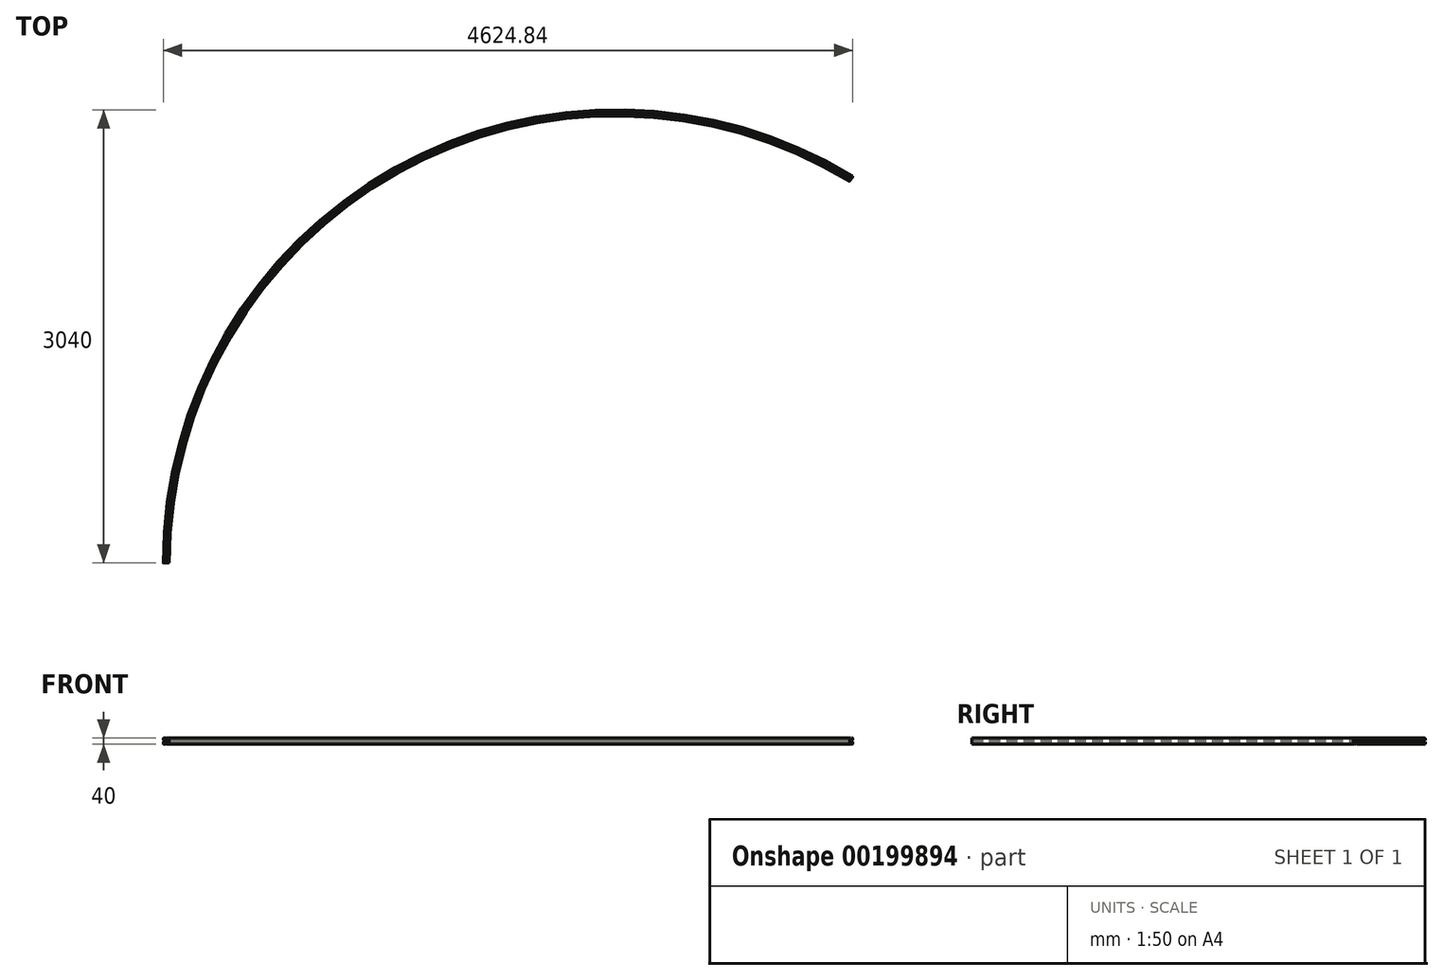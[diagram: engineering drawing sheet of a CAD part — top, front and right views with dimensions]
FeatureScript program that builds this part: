
annotation { "Feature Type Name" : "Feature", "Feature Type Description" : "" }
export const myFeature = defineFeature(function(context is Context, id is Id, definition is map)
    precondition{}
    {
        {
            var Q0;
            Q0=qCreatedBy(makeId("Front.planeOp"),FACE);
            var sketch = newSketch(context, id + "F0", { "sketchPlane" : qUnion([Q0])});
            skArc(sketch, "E0", {"start": v(20, 17) * mm, "mid": v(19.12, 19.12) * mm, "end": v(17, 20) * mm});
            skArc(sketch, "E1", {"start": v(10.03, 11.53) * mm, "mid": v(10.38, 12.05) * mm, "end": v(10.5, 12.66) * mm});
            skArc(sketch, "E2", {"start": v(5.34, 8.5) * mm, "mid": v(6.87, 8.8) * mm, "end": v(8.17, 9.67) * mm});
            skArc(sketch, "E3", {"start": v(-8.17, 9.67) * mm, "mid": v(-6.87, 8.8) * mm, "end": v(-5.34, 8.5) * mm});
            skArc(sketch, "E4", {"start": v(-10.5, 12.66) * mm, "mid": v(-10.38, 12.05) * mm, "end": v(-10.03, 11.53) * mm});
            skArc(sketch, "E5", {"start": v(-17, 20) * mm, "mid": v(-19.12, 19.12) * mm, "end": v(-20, 17) * mm});
            skArc(sketch, "E6", {"start": v(-11.53, 10.03) * mm, "mid": v(-12.05, 10.38) * mm, "end": v(-12.66, 10.5) * mm});
            skArc(sketch, "E7", {"start": v(-8.5, 5.34) * mm, "mid": v(-8.8, 6.87) * mm, "end": v(-9.67, 8.17) * mm});
            skArc(sketch, "E8", {"start": v(-9.67, -8.17) * mm, "mid": v(-8.8, -6.87) * mm, "end": v(-8.5, -5.34) * mm});
            skArc(sketch, "E9", {"start": v(-12.66, -10.5) * mm, "mid": v(-12.05, -10.38) * mm, "end": v(-11.53, -10.03) * mm});
            skArc(sketch, "E10", {"start": v(-20, -17) * mm, "mid": v(-19.12, -19.12) * mm, "end": v(-17, -20) * mm});
            skArc(sketch, "E11", {"start": v(-10.03, -11.53) * mm, "mid": v(-10.38, -12.05) * mm, "end": v(-10.5, -12.66) * mm});
            skArc(sketch, "E12", {"start": v(-5.34, -8.5) * mm, "mid": v(-6.87, -8.8) * mm, "end": v(-8.17, -9.67) * mm});
            skArc(sketch, "E13", {"start": v(8.17, -9.67) * mm, "mid": v(6.87, -8.8) * mm, "end": v(5.34, -8.5) * mm});
            skArc(sketch, "E14", {"start": v(10.5, -12.66) * mm, "mid": v(10.38, -12.05) * mm, "end": v(10.03, -11.53) * mm});
            skArc(sketch, "E15", {"start": v(10.8, -20) * mm, "mid": v(11.86, -19.56) * mm, "end": v(12.3, -18.5) * mm});
            skArc(sketch, "E16", {"start": v(16.5, -18.5) * mm, "mid": v(16.94, -19.56) * mm, "end": v(18, -20) * mm});
            skArc(sketch, "E17", {"start": v(18, -20) * mm, "mid": v(19.45, -18.9) * mm, "end": v(20, -17.17) * mm});
            skArc(sketch, "E18", {"start": v(-18.5, -17) * mm, "mid": v(-18.06, -18.06) * mm, "end": v(-17, -18.5) * mm});
            skArc(sketch, "E19", {"start": v(-1.15, 5.89) * mm, "mid": v(-2.27, 5.55) * mm, "end": v(-3.3, 5.01) * mm});
            skArc(sketch, "E20", {"start": v(3.3, 5.01) * mm, "mid": v(2.27, 5.55) * mm, "end": v(1.15, 5.89) * mm});
            skArc(sketch, "E21", {"start": v(5.89, 1.15) * mm, "mid": v(5.55, 2.27) * mm, "end": v(5.01, 3.3) * mm});
            skArc(sketch, "E22", {"start": v(5.01, -3.3) * mm, "mid": v(5.55, -2.27) * mm, "end": v(5.89, -1.15) * mm});
            skArc(sketch, "E23", {"start": v(8.41, -8.12) * mm, "mid": v(8.93, -8.15) * mm, "end": v(9.2, -7.7) * mm});
            skArc(sketch, "E24", {"start": v(8.41, -8.12) * mm, "mid": v(6.95, -7.4) * mm, "end": v(5.34, -7.15) * mm});
            skArc(sketch, "E25", {"start": v(1.15, -5.89) * mm, "mid": v(2.27, -5.55) * mm, "end": v(3.3, -5.01) * mm});
            skArc(sketch, "E26", {"start": v(-3.3, -5.01) * mm, "mid": v(-2.27, -5.55) * mm, "end": v(-1.15, -5.89) * mm});
            skArc(sketch, "E27", {"start": v(-5.89, -1.15) * mm, "mid": v(-5.55, -2.27) * mm, "end": v(-5.01, -3.3) * mm});
            skArc(sketch, "E28", {"start": v(-5.01, 3.3) * mm, "mid": v(-5.55, 2.27) * mm, "end": v(-5.89, 1.15) * mm});
            skArc(sketch, "E29", {"start": v(18.5, 17) * mm, "mid": v(18.06, 18.06) * mm, "end": v(17, 18.5) * mm});
            skArc(sketch, "E30", {"start": v(-17, 18.5) * mm, "mid": v(-18.06, 18.06) * mm, "end": v(-18.5, 17) * mm});
            skLineSegment(sketch, "E31", {"start": v(17, 20) * mm, "end": v(4.1, 20) * mm});
            skLineSegment(sketch, "E32", {"start": v(4.1, 20) * mm, "end": v(4.1, 17) * mm});
            skLineSegment(sketch, "E33", {"start": v(4.1, 17) * mm, "end": v(10.5, 17) * mm});
            skLineSegment(sketch, "E34", {"start": v(10.5, 17) * mm, "end": v(10.5, 12.66) * mm});
            skLineSegment(sketch, "E35", {"start": v(10.03, 11.53) * mm, "end": v(8.17, 9.67) * mm});
            skLineSegment(sketch, "E36", {"start": v(5.34, 8.5) * mm, "end": v(-5.34, 8.5) * mm});
            skLineSegment(sketch, "E37", {"start": v(-8.17, 9.67) * mm, "end": v(-10.03, 11.53) * mm});
            skLineSegment(sketch, "E38", {"start": v(-10.5, 12.66) * mm, "end": v(-10.5, 17) * mm});
            skLineSegment(sketch, "E39", {"start": v(-10.5, 17) * mm, "end": v(-4.1, 17) * mm});
            skLineSegment(sketch, "E40", {"start": v(-4.1, 17) * mm, "end": v(-4.1, 20) * mm});
            skLineSegment(sketch, "E41", {"start": v(-4.1, 20) * mm, "end": v(-17, 20) * mm});
            skLineSegment(sketch, "E42", {"start": v(-20, 17) * mm, "end": v(-20, 4.1) * mm});
            skLineSegment(sketch, "E43", {"start": v(-20, 4.1) * mm, "end": v(-17, 4.1) * mm});
            skLineSegment(sketch, "E44", {"start": v(-17, 4.1) * mm, "end": v(-17, 10.5) * mm});
            skLineSegment(sketch, "E45", {"start": v(-17, 10.5) * mm, "end": v(-12.66, 10.5) * mm});
            skLineSegment(sketch, "E46", {"start": v(-11.53, 10.03) * mm, "end": v(-9.67, 8.17) * mm});
            skLineSegment(sketch, "E47", {"start": v(-8.5, 5.34) * mm, "end": v(-8.5, -5.34) * mm});
            skLineSegment(sketch, "E48", {"start": v(-9.67, -8.17) * mm, "end": v(-11.53, -10.03) * mm});
            skLineSegment(sketch, "E49", {"start": v(-12.66, -10.5) * mm, "end": v(-17, -10.5) * mm});
            skLineSegment(sketch, "E50", {"start": v(-17, -10.5) * mm, "end": v(-17, -4.1) * mm});
            skLineSegment(sketch, "E51", {"start": v(-17, -4.1) * mm, "end": v(-20, -4.1) * mm});
            skLineSegment(sketch, "E52", {"start": v(-20, -4.1) * mm, "end": v(-20, -17) * mm});
            skLineSegment(sketch, "E53", {"start": v(-17, -20) * mm, "end": v(-4.1, -20) * mm});
            skLineSegment(sketch, "E54", {"start": v(-4.1, -20) * mm, "end": v(-4.1, -17) * mm});
            skLineSegment(sketch, "E55", {"start": v(-4.1, -17) * mm, "end": v(-10.5, -17) * mm});
            skLineSegment(sketch, "E56", {"start": v(-10.5, -17) * mm, "end": v(-10.5, -12.66) * mm});
            skLineSegment(sketch, "E57", {"start": v(-10.03, -11.53) * mm, "end": v(-8.17, -9.67) * mm});
            skLineSegment(sketch, "E58", {"start": v(-5.34, -8.5) * mm, "end": v(5.34, -8.5) * mm});
            skLineSegment(sketch, "E59", {"start": v(8.17, -9.67) * mm, "end": v(10.03, -11.53) * mm});
            skLineSegment(sketch, "E60", {"start": v(10.5, -12.66) * mm, "end": v(10.5, -17) * mm});
            skLineSegment(sketch, "E61", {"start": v(10.5, -17) * mm, "end": v(4.1, -17) * mm});
            skLineSegment(sketch, "E62", {"start": v(4.1, -17) * mm, "end": v(4.1, -20) * mm});
            skLineSegment(sketch, "E63", {"start": v(4.1, -20) * mm, "end": v(10.8, -20) * mm});
            skLineSegment(sketch, "E64", {"start": v(12.3, -18.5) * mm, "end": v(12.28, -15) * mm});
            skLineSegment(sketch, "E65", {"start": v(12.28, -15) * mm, "end": v(11.98, -15) * mm});
            skLineSegment(sketch, "E66", {"start": v(11.98, -15) * mm, "end": v(11.97, -11) * mm});
            skLineSegment(sketch, "E67", {"start": v(11.97, -11) * mm, "end": v(12.27, -11) * mm});
            skLineSegment(sketch, "E68", {"start": v(12.27, -11) * mm, "end": v(12.2, 7.5) * mm});
            skLineSegment(sketch, "E69", {"start": v(12.2, 7.5) * mm, "end": v(16.6, 7.5) * mm});
            skLineSegment(sketch, "E70", {"start": v(16.6, 7.5) * mm, "end": v(16.53, -11) * mm});
            skLineSegment(sketch, "E71", {"start": v(16.53, -11) * mm, "end": v(16.83, -11) * mm});
            skLineSegment(sketch, "E72", {"start": v(16.83, -11) * mm, "end": v(16.82, -15) * mm});
            skLineSegment(sketch, "E73", {"start": v(16.82, -15) * mm, "end": v(16.52, -15) * mm});
            skLineSegment(sketch, "E74", {"start": v(16.52, -15) * mm, "end": v(16.5, -18.5) * mm});
            skLineSegment(sketch, "E75", {"start": v(-12, -18.5) * mm, "end": v(-12, -12) * mm});
            skLineSegment(sketch, "E76", {"start": v(-17, -18.5) * mm, "end": v(-12, -18.5) * mm});
            skLineSegment(sketch, "E77", {"start": v(-18.5, -12) * mm, "end": v(-18.5, -17) * mm});
            skLineSegment(sketch, "E78", {"start": v(-4.2, 7.15) * mm, "end": v(-7.15, 7.15) * mm});
            skLineSegment(sketch, "E79", {"start": v(-4.2, 5.9) * mm, "end": v(-4.2, 7.15) * mm});
            skLineSegment(sketch, "E80", {"start": v(-3.3, 5.01) * mm, "end": v(-4.2, 5.9) * mm});
            skLineSegment(sketch, "E81", {"start": v(-1.15, 7.15) * mm, "end": v(-1.15, 5.89) * mm});
            skLineSegment(sketch, "E82", {"start": v(1.15, 7.15) * mm, "end": v(-1.15, 7.15) * mm});
            skLineSegment(sketch, "E83", {"start": v(1.15, 5.89) * mm, "end": v(1.15, 7.15) * mm});
            skLineSegment(sketch, "E84", {"start": v(4.2, 5.9) * mm, "end": v(3.3, 5.01) * mm});
            skLineSegment(sketch, "E85", {"start": v(4.2, 7.15) * mm, "end": v(4.2, 5.9) * mm});
            skLineSegment(sketch, "E86", {"start": v(9.2, 7.15) * mm, "end": v(4.2, 7.15) * mm});
            skLineSegment(sketch, "E87", {"start": v(9.2, 4.2) * mm, "end": v(9.2, 7.15) * mm});
            skLineSegment(sketch, "E88", {"start": v(5.9, 4.2) * mm, "end": v(9.2, 4.2) * mm});
            skLineSegment(sketch, "E89", {"start": v(5.01, 3.3) * mm, "end": v(5.9, 4.2) * mm});
            skLineSegment(sketch, "E90", {"start": v(9.2, 1.15) * mm, "end": v(5.89, 1.15) * mm});
            skLineSegment(sketch, "E91", {"start": v(9.2, -1.15) * mm, "end": v(9.2, 1.15) * mm});
            skLineSegment(sketch, "E92", {"start": v(5.89, -1.15) * mm, "end": v(9.2, -1.15) * mm});
            skLineSegment(sketch, "E93", {"start": v(5.9, -4.2) * mm, "end": v(5.01, -3.3) * mm});
            skLineSegment(sketch, "E94", {"start": v(9.2, -4.2) * mm, "end": v(5.9, -4.2) * mm});
            skLineSegment(sketch, "E95", {"start": v(9.2, -7.7) * mm, "end": v(9.2, -4.2) * mm});
            skLineSegment(sketch, "E96", {"start": v(4.2, -7.15) * mm, "end": v(5.34, -7.15) * mm});
            skLineSegment(sketch, "E97", {"start": v(4.2, -5.9) * mm, "end": v(4.2, -7.15) * mm});
            skLineSegment(sketch, "E98", {"start": v(3.3, -5.01) * mm, "end": v(4.2, -5.9) * mm});
            skLineSegment(sketch, "E99", {"start": v(1.15, -7.15) * mm, "end": v(1.15, -5.89) * mm});
            skLineSegment(sketch, "E100", {"start": v(-1.15, -7.15) * mm, "end": v(1.15, -7.15) * mm});
            skLineSegment(sketch, "E101", {"start": v(-1.15, -5.89) * mm, "end": v(-1.15, -7.15) * mm});
            skLineSegment(sketch, "E102", {"start": v(-4.2, -5.9) * mm, "end": v(-3.3, -5.01) * mm});
            skLineSegment(sketch, "E103", {"start": v(-4.2, -7.15) * mm, "end": v(-4.2, -5.9) * mm});
            skLineSegment(sketch, "E104", {"start": v(-7.15, -7.15) * mm, "end": v(-4.2, -7.15) * mm});
            skLineSegment(sketch, "E105", {"start": v(-7.15, -4.2) * mm, "end": v(-7.15, -7.15) * mm});
            skLineSegment(sketch, "E106", {"start": v(-5.9, -4.2) * mm, "end": v(-7.15, -4.2) * mm});
            skLineSegment(sketch, "E107", {"start": v(-5.01, -3.3) * mm, "end": v(-5.9, -4.2) * mm});
            skLineSegment(sketch, "E108", {"start": v(-7.15, -1.15) * mm, "end": v(-5.89, -1.15) * mm});
            skLineSegment(sketch, "E109", {"start": v(-7.15, 1.15) * mm, "end": v(-7.15, -1.15) * mm});
            skLineSegment(sketch, "E110", {"start": v(-5.89, 1.15) * mm, "end": v(-7.15, 1.15) * mm});
            skLineSegment(sketch, "E111", {"start": v(-5.9, 4.2) * mm, "end": v(-5.01, 3.3) * mm});
            skLineSegment(sketch, "E112", {"start": v(-7.15, 4.2) * mm, "end": v(-5.9, 4.2) * mm});
            skLineSegment(sketch, "E113", {"start": v(-12, 18.5) * mm, "end": v(-17, 18.5) * mm});
            skLineSegment(sketch, "E114", {"start": v(-12, 12) * mm, "end": v(-12, 18.5) * mm});
            skLineSegment(sketch, "E115", {"start": v(-18.5, 12) * mm, "end": v(-12, 12) * mm});
            skLineSegment(sketch, "E116", {"start": v(-18.5, 17) * mm, "end": v(-18.5, 12) * mm});
            skLineSegment(sketch, "E117", {"start": v(17, 18.5) * mm, "end": v(12, 18.5) * mm});
            skLineSegment(sketch, "E118", {"start": v(18.5, 12) * mm, "end": v(18.5, 17) * mm});
            skLineSegment(sketch, "E119", {"start": v(12, 12) * mm, "end": v(18.5, 12) * mm});
            skLineSegment(sketch, "E120", {"start": v(-12, -12) * mm, "end": v(-18.5, -12) * mm});
            skLineSegment(sketch, "E121", {"start": v(-7.15, 7.15) * mm, "end": v(-7.15, 4.2) * mm});
            skLineSegment(sketch, "E122", {"start": v(12, 18.5) * mm, "end": v(12, 12) * mm});
            skLineSegment(sketch, "E123", {"start": v(20, -17.17) * mm, "end": v(20, 17) * mm});
            skLineSegment(sketch, "E124", {"start": v(18, 20) * mm, "end": v(21, 20) * mm});
            skLineSegment(sketch, "E125", {"start": v(20, 18) * mm, "end": v(20, 21) * mm});
            skLineSegment(sketch, "E126", {"start": v(-18, 20) * mm, "end": v(-21, 20) * mm});
            skLineSegment(sketch, "E127", {"start": v(-20, 18) * mm, "end": v(-20, 21) * mm});
            skLineSegment(sketch, "E128", {"start": v(-18, -20) * mm, "end": v(-21, -20) * mm});
            skLineSegment(sketch, "E129", {"start": v(-20, -18) * mm, "end": v(-20, -21) * mm});
            skLineSegment(sketch, "E130", {"start": v(-3.1, -20) * mm, "end": v(21, -20) * mm});
            skLineSegment(sketch, "E131", {"start": v(20, -18.17) * mm, "end": v(20, -21) * mm});
            skSolve(sketch);
        }
        {
            var Q0;
            Q0=qCreatedBy(makeId("Top.planeOp"),FACE);
            var sketch = newSketch(context, id + "F1", { "sketchPlane" : qUnion([Q0])});
            skArc(sketch, "E132", {"start": v(0, 0) * mm, "mid": v(1542.56, 2633.93) * mm, "end": v(4594.42, 2577.13) * mm});
            skLineSegment(sketch, "E133", {"start": v(0, 0) * mm, "end": v(3020, 0) * mm, "construction": true});
            skLineSegment(sketch, "E134", {"start": v(4594.42, 2577.13) * mm, "end": v(3020, 0) * mm, "construction": true});
            skSolve(sketch);
        }
        {
            var Q0;
            Q0=makeQuery(id+"F0.imprint","IMPRINT",FACE,{"disambiguationData":[TD([[makeQuery(id+"F0.imprint","IMPRINT",EDGE,{"derivedFrom":sQuery(id+"F0.wireOp",EDGE,"E0")}),1.0]])]});
            var Q1;
            Q1=sQuery(id+"F1.wireOp",EDGE,"E132");
            sweep(context, id + "F2", {"profiles" : qUnion([Q0]), "path" : qUnion([Q1])});
        }
    });
